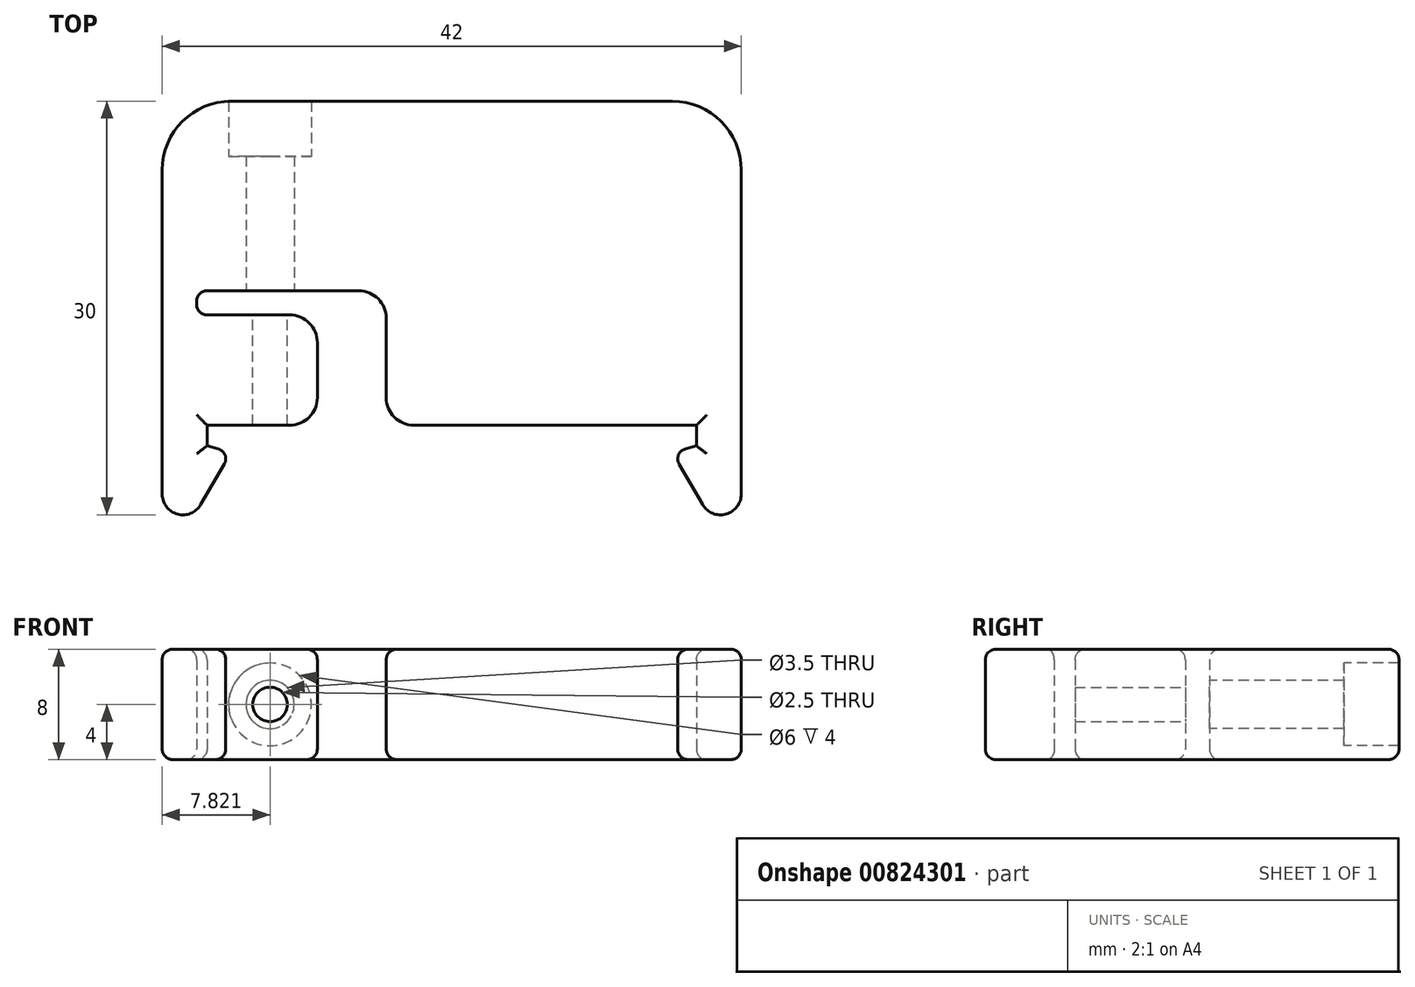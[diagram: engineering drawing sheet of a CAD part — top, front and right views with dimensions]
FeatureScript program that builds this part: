
annotation { "Feature Type Name" : "Feature", "Feature Type Description" : "" }
export const myFeature = defineFeature(function(context is Context, id is Id, definition is map)
    precondition{}
    {
        {
            var Q0;
            Q0=qCreatedBy(makeId("Top.planeOp"),FACE);
            var sketch = newSketch(context, id + "F0", { "sketchPlane" : qUnion([Q0])});
            skLineSegment(sketch, "E0", {"start": v(-17.75, 0) * mm, "end": v(-9.75, 0) * mm});
            skLineSegment(sketch, "E1", {"start": v(17.75, 0) * mm, "end": v(17.75, -1.5) * mm});
            skLineSegment(sketch, "E2", {"start": v(17.75, -1.5) * mm, "end": v(16, -1.97) * mm});
            skLineSegment(sketch, "E3", {"start": v(-16, -1.97) * mm, "end": v(-17.75, -1.5) * mm});
            skLineSegment(sketch, "E4", {"start": v(-17.75, -1.5) * mm, "end": v(-17.75, 0) * mm});
            skLineSegment(sketch, "E5", {"start": v(17.75, 0) * mm, "end": v(-4.75, 0) * mm});
            skLineSegment(sketch, "E6", {"start": v(0, 25.54) * mm, "end": v(0, -8.71) * mm, "construction": true});
            skLineSegment(sketch, "E7", {"start": v(-16, -1.97) * mm, "end": v(-18.2, -5.75) * mm});
            skLineSegment(sketch, "E8", {"start": v(-21, -5) * mm, "end": v(-21, 23.5) * mm});
            skLineSegment(sketch, "E9", {"start": v(-9.75, 0) * mm, "end": v(-9.75, 8) * mm});
            skLineSegment(sketch, "E10", {"start": v(-9.75, 8) * mm, "end": v(-18.5, 8) * mm});
            skLineSegment(sketch, "E11", {"start": v(-18.5, 8) * mm, "end": v(-18.5, 9.75) * mm});
            skLineSegment(sketch, "E12", {"start": v(-18.5, 9.75) * mm, "end": v(-4.75, 9.75) * mm});
            skLineSegment(sketch, "E13", {"start": v(-4.75, 9.75) * mm, "end": v(-4.75, 0) * mm});
            skLineSegment(sketch, "E14", {"start": v(16, -1.97) * mm, "end": v(18.2, -5.75) * mm});
            skLineSegment(sketch, "E15", {"start": v(21, -5) * mm, "end": v(21, 23.5) * mm});
            skLineSegment(sketch, "E16", {"start": v(-21, 23.5) * mm, "end": v(21, 23.5) * mm});
            skPoint(sketch, "E17.visualSharp", {"position": v(-21, -10.56) * mm});
            skArc(sketch, "E17.filletArc", {"start": v(-21, -5) * mm, "mid": v(-19.9, -6.45) * mm, "end": v(-18.2, -5.75) * mm});
            skPoint(sketch, "E18.visualSharp", {"position": v(21, -10.56) * mm});
            skArc(sketch, "E18.filletArc", {"start": v(18.2, -5.75) * mm, "mid": v(19.9, -6.45) * mm, "end": v(21, -5) * mm});
            skSolve(sketch);
        }
        {
            var Q0;
            Q0 = qSketchRegion(id + "F0", true);
            extrude(context, id + "F1", {"entities" : qUnion([Q0]), "depth" : 8 * mm, "offsetDistance" : 25 * mm, "symmetric" : true});
        }
        {
            var Q0;
            Q0=makeQuery(id+"F1.opExtrude","SWEPT_FACE",FACE,{"disambiguationData":[OSD([sQuery(id+"F0.wireOp",EDGE,"E10")])]});
            var sketch = newSketch(context, id + "F2", { "sketchPlane" : qUnion([Q0])});
            skCircle(sketch, "E19", {"center": v(13.18, 0) * mm, "radius": 1.25 * mm});
            skSolve(sketch);
        }
        {
            var Q0;
            Q0 = qSketchRegion(id + "F2", true);
            extrude(context, id + "F3", {"entities" : qUnion([Q0]), "operationType" : NewBodyOperationType.REMOVE, "endBound" : BoundingType.THROUGH_ALL, "oppositeDirection" : true, "depth" : 25 * mm, "offsetDistance" : 25 * mm});
        }
        {
            var Q0;
            Q0=makeQuery(id+"F1.opExtrude","SWEPT_FACE",FACE,{"disambiguationData":[OSD([sQuery(id+"F0.wireOp",EDGE,"E12")])]});
            var sketch = newSketch(context, id + "F4", { "sketchPlane" : qUnion([Q0])});
            skCircle(sketch, "E20", {"center": v(-13.18, 0) * mm, "radius": 1.75 * mm});
            skSolve(sketch);
        }
        {
            var Q0;
            Q0 = qSketchRegion(id + "F4", true);
            extrude(context, id + "F5", {"entities" : qUnion([Q0]), "operationType" : NewBodyOperationType.REMOVE, "endBound" : BoundingType.THROUGH_ALL, "oppositeDirection" : true, "depth" : 25 * mm, "offsetDistance" : 25 * mm});
        }
        {
            var Q0;
            Q0=makeQuery(id+"F1.opExtrude","SWEPT_FACE",FACE,{"disambiguationData":[OSD([sQuery(id+"F0.wireOp",EDGE,"E16")])]});
            cPlane(context, id + "F6", {"entities" : qUnion([Q0]), "cplaneType" : CPlaneType.OFFSET, "offset" : 4 * mm, "oppositeDirection" : true, "width" : 150 * mm, "height" : 150 * mm});
        }
        {
            var Q0;
            Q0=qCreatedBy(id+"F6.planeOp",FACE);
            var sketch = newSketch(context, id + "F7", { "sketchPlane" : qUnion([Q0])});
            skCircle(sketch, "E21", {"center": v(13.18, 0) * mm, "radius": 3 * mm});
            skSolve(sketch);
        }
        {
            var Q0;
            Q0 = qSketchRegion(id + "F7", true);
            extrude(context, id + "F8", {"entities" : qUnion([Q0]), "operationType" : NewBodyOperationType.REMOVE, "endBound" : BoundingType.THROUGH_ALL, "depth" : 25 * mm, "offsetDistance" : 25 * mm});
        }
        {
            var Q0;
            Q0=makeQuery(id+"F1.opExtrude","SWEPT_EDGE",EDGE,{"disambiguationData":[OSD([sQuery(id+"F0.wireOp",EDGE,"E8"),sQuery(id+"F0.wireOp",EDGE,"E16")])]});
            var Q1;
            Q1=makeQuery(id+"F1.opExtrude","SWEPT_EDGE",EDGE,{"disambiguationData":[OSD([sQuery(id+"F0.wireOp",EDGE,"E15"),sQuery(id+"F0.wireOp",EDGE,"E16")])]});
            fillet(context, id + "F9", {"entities" : qUnion([Q0, Q1]), "radius" : 5 * mm, "tangentPropagation" : true, "allowEdgeOverflow" : false});
        }
        {
            var Q0;
            Q0=makeQuery(id+"F1.opExtrude","SWEPT_EDGE",EDGE,{"disambiguationData":[OSD([sQuery(id+"F0.wireOp",EDGE,"E5"),sQuery(id+"F0.wireOp",EDGE,"E13")])]});
            var Q1;
            Q1=makeQuery(id+"F1.opExtrude","SWEPT_EDGE",EDGE,{"disambiguationData":[OSD([sQuery(id+"F0.wireOp",EDGE,"E0"),sQuery(id+"F0.wireOp",EDGE,"E9")])]});
            var Q2;
            Q2=makeQuery(id+"F1.opExtrude","SWEPT_EDGE",EDGE,{"disambiguationData":[OSD([sQuery(id+"F0.wireOp",EDGE,"E9"),sQuery(id+"F0.wireOp",EDGE,"E10")])]});
            var Q3;
            Q3=makeQuery(id+"F1.opExtrude","SWEPT_EDGE",EDGE,{"disambiguationData":[OSD([sQuery(id+"F0.wireOp",EDGE,"E12"),sQuery(id+"F0.wireOp",EDGE,"E13")])]});
            fillet(context, id + "F10", {"entities" : qUnion([Q0, Q1, Q2, Q3]), "radius" : 2 * mm, "tangentPropagation" : true, "allowEdgeOverflow" : false});
        }
        {
            var Q0;
            Q0=makeQuery(id+"F1.opExtrude","SWEPT_EDGE",EDGE,{"disambiguationData":[OSD([sQuery(id+"F0.wireOp",EDGE,"E3"),sQuery(id+"F0.wireOp",EDGE,"E7")])]});
            var Q1;
            Q1=makeQuery(id+"F1.opExtrude","SWEPT_EDGE",EDGE,{"disambiguationData":[OSD([sQuery(id+"F0.wireOp",EDGE,"E2"),sQuery(id+"F0.wireOp",EDGE,"E14")])]});
            var Q2;
            Q2=makeQuery(id+"F1.opExtrude","SWEPT_EDGE",EDGE,{"disambiguationData":[OSD([sQuery(id+"F0.wireOp",EDGE,"E11"),sQuery(id+"F0.wireOp",EDGE,"E12")])]});
            var Q3;
            Q3=makeQuery(id+"F1.opExtrude","SWEPT_EDGE",EDGE,{"disambiguationData":[OSD([sQuery(id+"F0.wireOp",EDGE,"E10"),sQuery(id+"F0.wireOp",EDGE,"E11")])]});
            var Q4;
            Q4=makeQuery(id+"F1.opExtrude","CAP_FACE",FACE,{"disambiguationData":[OSD([sQuery(id+"F0.wireOp",EDGE,"E0"),sQuery(id+"F0.wireOp",EDGE,"E1"),sQuery(id+"F0.wireOp",EDGE,"E2"),sQuery(id+"F0.wireOp",EDGE,"E3"),sQuery(id+"F0.wireOp",EDGE,"E4"),sQuery(id+"F0.wireOp",EDGE,"E5"),sQuery(id+"F0.wireOp",EDGE,"E7"),sQuery(id+"F0.wireOp",EDGE,"E8"),sQuery(id+"F0.wireOp",EDGE,"E9"),sQuery(id+"F0.wireOp",EDGE,"E10"),sQuery(id+"F0.wireOp",EDGE,"E11"),sQuery(id+"F0.wireOp",EDGE,"E12"),sQuery(id+"F0.wireOp",EDGE,"E13"),sQuery(id+"F0.wireOp",EDGE,"E14"),sQuery(id+"F0.wireOp",EDGE,"E15"),sQuery(id+"F0.wireOp",EDGE,"E16"),sQuery(id+"F0.wireOp",EDGE,"E17.filletArc"),sQuery(id+"F0.wireOp",EDGE,"E18.filletArc")])],"isStart":false});
            var Q5;
            Q5=makeQuery(id+"F1.opExtrude","CAP_FACE",FACE,{"disambiguationData":[OSD([sQuery(id+"F0.wireOp",EDGE,"E0"),sQuery(id+"F0.wireOp",EDGE,"E1"),sQuery(id+"F0.wireOp",EDGE,"E2"),sQuery(id+"F0.wireOp",EDGE,"E3"),sQuery(id+"F0.wireOp",EDGE,"E4"),sQuery(id+"F0.wireOp",EDGE,"E5"),sQuery(id+"F0.wireOp",EDGE,"E7"),sQuery(id+"F0.wireOp",EDGE,"E8"),sQuery(id+"F0.wireOp",EDGE,"E9"),sQuery(id+"F0.wireOp",EDGE,"E10"),sQuery(id+"F0.wireOp",EDGE,"E11"),sQuery(id+"F0.wireOp",EDGE,"E12"),sQuery(id+"F0.wireOp",EDGE,"E13"),sQuery(id+"F0.wireOp",EDGE,"E14"),sQuery(id+"F0.wireOp",EDGE,"E15"),sQuery(id+"F0.wireOp",EDGE,"E16"),sQuery(id+"F0.wireOp",EDGE,"E17.filletArc"),sQuery(id+"F0.wireOp",EDGE,"E18.filletArc")])],"isStart":true});
            fillet(context, id + "F11", {"entities" : qUnion([Q0, Q1, Q2, Q3, Q4, Q5]), "radius" : 0.75 * mm, "tangentPropagation" : true, "allowEdgeOverflow" : false});
        }
    });
